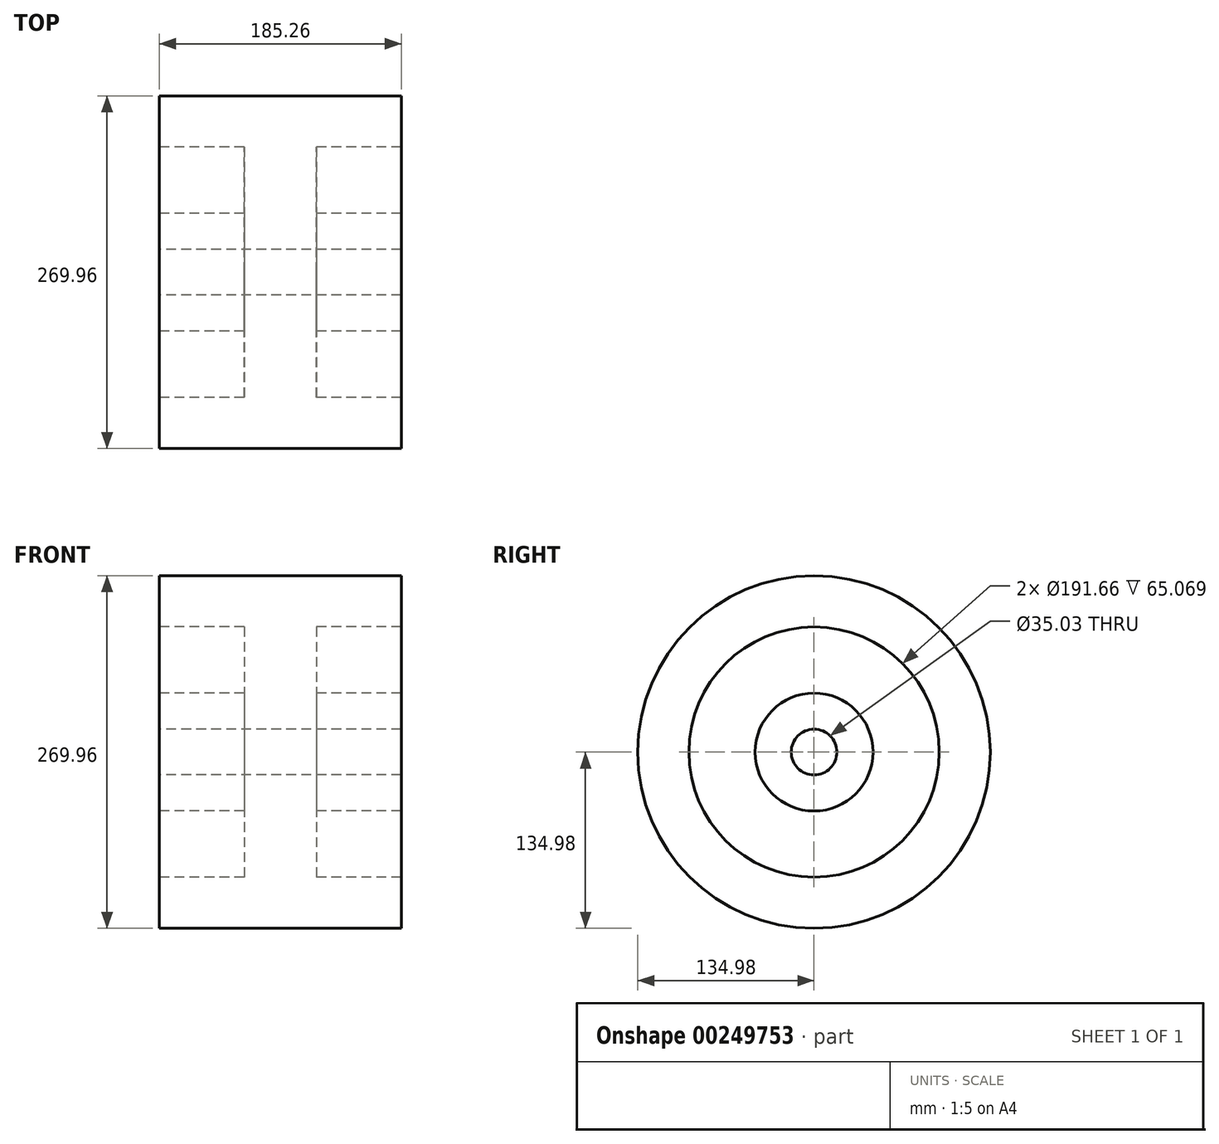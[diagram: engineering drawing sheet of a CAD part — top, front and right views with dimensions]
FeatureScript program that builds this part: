
annotation { "Feature Type Name" : "Feature", "Feature Type Description" : "" }
export const myFeature = defineFeature(function(context is Context, id is Id, definition is map)
    precondition{}
    {
        {
            var Q0;
            Q0=qCreatedBy(makeId("Front.planeOp"),FACE);
            var sketch = newSketch(context, id + "F0", { "sketchPlane" : qUnion([Q0])});
            skLineSegment(sketch, "E0", {"start": v(-132.1, 0) * mm, "end": v(131.6, 0) * mm, "construction": true});
            skLineSegment(sketch, "E1", {"start": v(0, 0) * mm, "end": v(0, 205.5) * mm, "construction": true});
            skLineSegment(sketch, "E2", {"start": v(0, 134.98) * mm, "end": v(92.63, 134.98) * mm});
            skLineSegment(sketch, "E3", {"start": v(92.63, 134.98) * mm, "end": v(92.63, 95.83) * mm});
            skLineSegment(sketch, "E4", {"start": v(92.63, 95.83) * mm, "end": v(27.56, 95.83) * mm});
            skLineSegment(sketch, "E5", {"start": v(27.56, 95.83) * mm, "end": v(27.56, 45.15) * mm});
            skLineSegment(sketch, "E6", {"start": v(27.56, 45.15) * mm, "end": v(92.63, 45.15) * mm});
            skLineSegment(sketch, "E7", {"start": v(92.63, 45.15) * mm, "end": v(92.63, 17.51) * mm});
            skLineSegment(sketch, "E8", {"start": v(92.63, 17.51) * mm, "end": v(0, 17.51) * mm});
            skLineSegment(sketch, "E9.MirrorCS", {"start": v(0, 134.98) * mm, "end": v(-92.63, 134.98) * mm});
            skLineSegment(sketch, "E10.MirrorCS", {"start": v(-92.63, 134.98) * mm, "end": v(-92.63, 95.83) * mm});
            skLineSegment(sketch, "E11.MirrorCS", {"start": v(-27.56, 95.83) * mm, "end": v(-27.56, 45.15) * mm});
            skLineSegment(sketch, "E12.MirrorCS", {"start": v(-92.63, 95.83) * mm, "end": v(-27.56, 95.83) * mm});
            skLineSegment(sketch, "E13.MirrorCS", {"start": v(-27.56, 45.15) * mm, "end": v(-92.63, 45.15) * mm});
            skLineSegment(sketch, "E14.MirrorCS", {"start": v(-92.63, 17.51) * mm, "end": v(0, 17.51) * mm});
            skLineSegment(sketch, "E15.MirrorCS", {"start": v(-92.63, 45.15) * mm, "end": v(-92.63, 17.51) * mm});
            skSolve(sketch);
        }
        {
            var Q0;
            Q0=makeQuery(id+"F0.imprint","IMPRINT",FACE,{"disambiguationData":[TD([[makeQuery(id+"F0.imprint","IMPRINT",EDGE,{"derivedFrom":sQuery(id+"F0.wireOp",EDGE,"E2")}),-1.0]])]});
            var Q1;
            Q1=sQuery(id+"F0.wireOp",EDGE,"E0");
            revolve(context, id + "F1", {"entities" : qUnion([Q0]), "axis" : qUnion([Q1]), "revolveType" : RevolveType.FULL});
        }
    });
